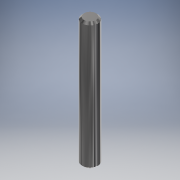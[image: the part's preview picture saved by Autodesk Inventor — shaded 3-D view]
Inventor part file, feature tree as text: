
AUTODESK INVENTOR PART (.ipt)
format: ipt  version: 2018 (Build 220112000, 112)  size: 125,440 bytes
history: native  units: mm (DEFAULTED — no unit token found)
features: extrude x1, chamfer x1, sketch x1
ambient origin geometry x8: Origin, YZ Plane, XZ Plane, XY Plane, X Axis, Y Axis, Z Axis, Center Point
bodies: Solid1 (feature_tree)
feature tree (3):
  extrude  "Extrusion1"  Depth=32.0mm TaperAngle=0.0deg
  chamfer  "Chamfer1"  Distance=0.5mm
  sketch  "Sketch1"  dims[d0=4.0mm d1=32.0mm d2=0.0mm d3=0.5mm d4=0.5mm d5=45.0deg]
